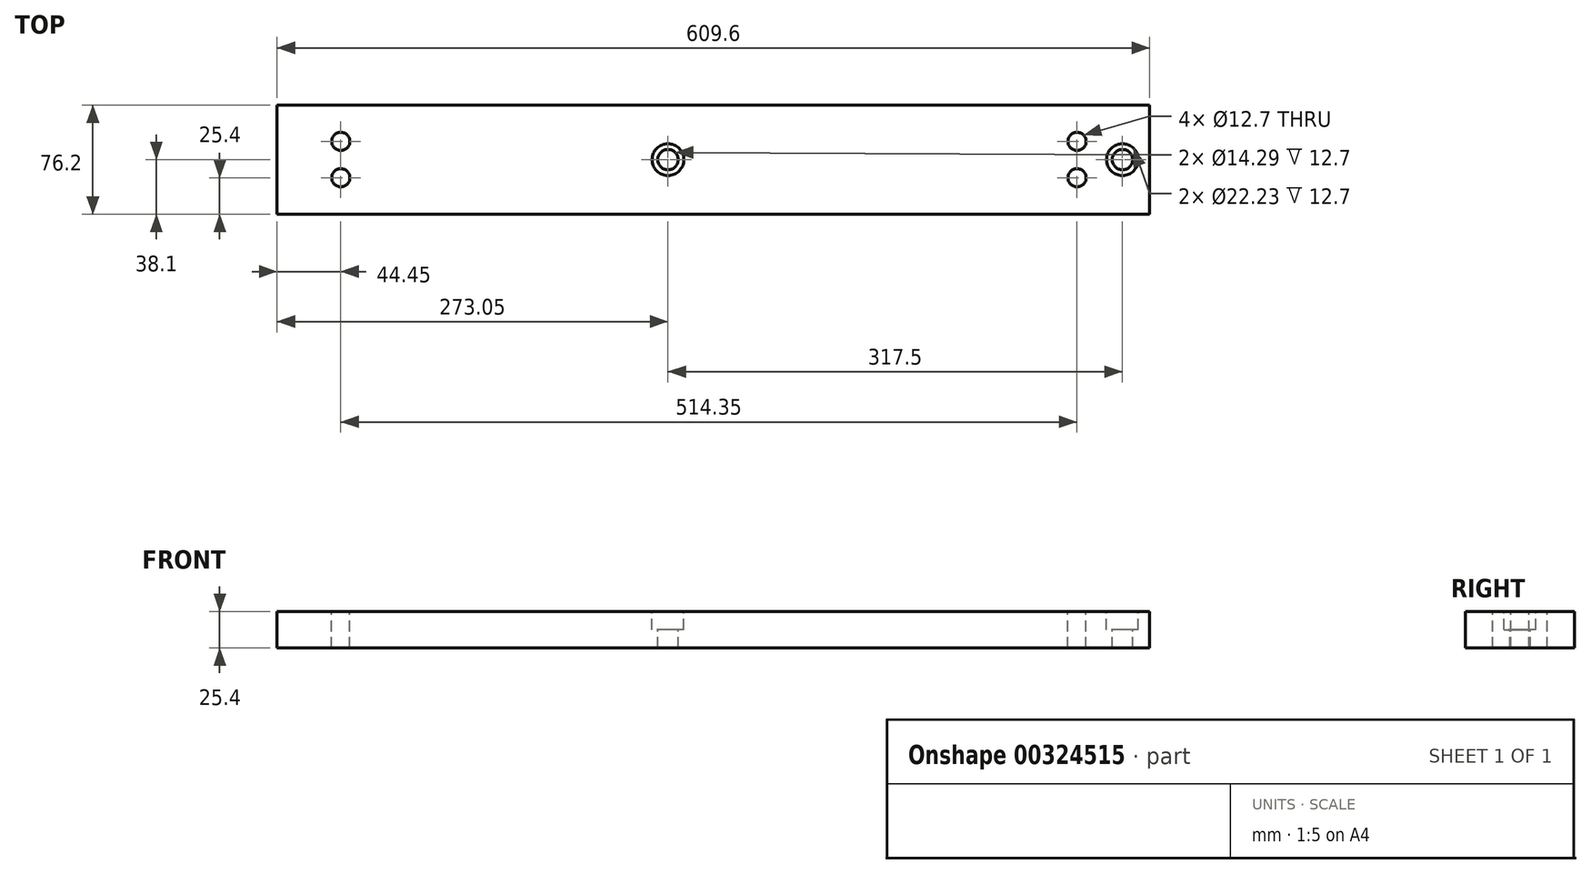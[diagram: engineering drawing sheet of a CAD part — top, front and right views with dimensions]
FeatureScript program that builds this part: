
annotation { "Feature Type Name" : "Feature", "Feature Type Description" : "" }
export const myFeature = defineFeature(function(context is Context, id is Id, definition is map)
    precondition{}
    {
        {
            var Q0;
            Q0=qCreatedBy(makeId("Top.planeOp"),FACE);
            var sketch = newSketch(context, id + "F0", { "sketchPlane" : qUnion([Q0])});
            skLineSegment(sketch, "E0.bottom", {"start": v(304.8, 38.1) * mm, "end": v(-304.8, 38.1) * mm});
            skLineSegment(sketch, "E0.top", {"start": v(304.8, -38.1) * mm, "end": v(-304.8, -38.1) * mm});
            skLineSegment(sketch, "E0.left", {"start": v(304.8, 38.1) * mm, "end": v(304.8, -38.1) * mm});
            skLineSegment(sketch, "E0.right", {"start": v(-304.8, 38.1) * mm, "end": v(-304.8, -38.1) * mm});
            skPoint(sketch, "E0.middle", {"position": v(0, 0) * mm});
            skSolve(sketch);
        }
        {
            var Q0;
            Q0 = qSketchRegion(id + "F0", true);
            extrude(context, id + "F1", {"entities" : qUnion([Q0]), "depth" : 25.4 * mm});
        }
        {
            var Q0;
            Q0=makeQuery(id+"F1.opExtrude","CAP_FACE",FACE,{"disambiguationData":[OSD([sQuery(id+"F0.wireOp",EDGE,"E0.bottom"),sQuery(id+"F0.wireOp",EDGE,"E0.top"),sQuery(id+"F0.wireOp",EDGE,"E0.left"),sQuery(id+"F0.wireOp",EDGE,"E0.right")])],"isStart":false});
            var sketch = newSketch(context, id + "F2", { "sketchPlane" : qUnion([Q0])});
            skLineSegment(sketch, "E1", {"start": v(304.8, 0) * mm, "end": v(198.42, 0) * mm, "construction": true});
            skPoint(sketch, "E1.endSnap0", {"position": v(304.8, 0) * mm});
            skCircle(sketch, "E2", {"center": v(254, -12.7) * mm, "radius": 6.35 * mm});
            skCircle(sketch, "E3.MirrorC", {"center": v(254, 12.7) * mm, "radius": 6.35 * mm});
            skCircle(sketch, "E4", {"center": v(-260.35, -12.7) * mm, "radius": 6.35 * mm});
            skCircle(sketch, "E5.MirrorC", {"center": v(-260.35, 12.7) * mm, "radius": 6.35 * mm});
            skSolve(sketch);
        }
        {
            var Q0;
            Q0 = qSketchRegion(id + "F2", true);
            extrude(context, id + "F3", {"entities" : qUnion([Q0]), "operationType" : NewBodyOperationType.REMOVE, "oppositeDirection" : true, "depth" : 25.4 * mm});
        }
        {
            var Q0;
            Q0=makeQuery(id+"F1.opExtrude","CAP_FACE",FACE,{"disambiguationData":[OSD([sQuery(id+"F0.wireOp",EDGE,"E0.bottom"),sQuery(id+"F0.wireOp",EDGE,"E0.top"),sQuery(id+"F0.wireOp",EDGE,"E0.left"),sQuery(id+"F0.wireOp",EDGE,"E0.right")])],"isStart":false});
            var sketch = newSketch(context, id + "F4", { "sketchPlane" : qUnion([Q0])});
            skLineSegment(sketch, "E6", {"start": v(304.8, 0) * mm, "end": v(285.75, 0) * mm, "construction": true});
            skLineSegment(sketch, "E7", {"start": v(285.75, 0) * mm, "end": v(-31.75, 0) * mm, "construction": true});
            skPoint(sketch, "E7.endSnap0", {"position": v(285.75, 0) * mm});
            skCircle(sketch, "E8.0", {"center": v(254, 12.7) * mm, "radius": 6.35 * mm, "construction": true});
            skSolve(sketch);
        }
        {
            var Q0;
            Q0=sQuery(id+"F4.wireOp",VERTEX,"E7.end");
            var Q1;
            Q1=sQuery(id+"F4.wireOp",VERTEX,"E6.end");
            var Q2;
            Q2=makeQuery(id+"F1.opExtrude","SWEPT_BODY",BODY,{"disambiguationData":[OSD([sQuery(id+"F0.wireOp",EDGE,"E0.bottom"),sQuery(id+"F0.wireOp",EDGE,"E0.top"),sQuery(id+"F0.wireOp",EDGE,"E0.left"),sQuery(id+"F0.wireOp",EDGE,"E0.right")])]});
            hole(context, id + "F5", {"style" : HoleStyle.C_BORE, "endStyle" : HoleEndStyle.THROUGH, "holeDiameter" : 14.29 * mm, "cBoreDiameter" : 22.22 * mm, "cBoreDepth" : 12.7 * mm, "tappedDepth" : 12.7 * mm, "tapClearance" : 3, "startFromSketch" : true, "locations" : qUnion([Q0, Q1]), "scope" : qUnion([Q2])});
        }
    });
